# Revit family: WT02 RHO
name_source: partatom
category: Windows
revit_build: Autodesk Revit Architecture 2012 (Build: 20110916_2132(x64)
units: mm (PartAtom-declared; Revit-internal decimal feet)

## types (4) — shared parameters
Casement Width = 395 mm
Cavity Closer Depth = 85 mm  [stored 0.278871 ft]
Cavity Closer Offset from Ext = 102.5 mm
Cavity Closer Width = 50 mm  [stored 0.164042 ft]
Cill Depth = 87.5 mm
Default Head Height = 2110 mm
Frame Depth = 65 mm
FrameOffset - External = 50 mm  [stored 0.164042 ft]
Glazing Thickness = 24 mm
Height = 1360 mm  [stored 4.46194 ft]
Keynote = L10
Manufacturer = Revit
Material Frame = Window Frame
Material Glass = Glass
Material Trim = Window Frame
Operation = DoublePanelVertical
Precast Width = 150 mm
Rough Height = 1130 mm
Vis - Cavity Closers = Yes
Wall Closure = By host
Window Board Extension = 25 mm  [stored 0.082021 ft]
Window Board Projection = 25 mm  [stored 0.082021 ft]
Wrap Layers (Ext) from Ext = 102.5 mm
Wrap Layers (Int) from Ext = 177.5 mm
window width = 935 mm

## per-type parameters (varying)
| type | Rough Width | Width |
| 1360x1360mm | 1500 mm | 1500 mm |
| 1360x1360mm 2 | 1360 mm  [stored 4.46194 ft] | 1360 mm  [stored 4.46194 ft] |
| 1360x1360mm (test) | 1360 mm  [stored 4.46194 ft] | 1360 mm  [stored 4.46194 ft] |
| 1360x1360mm (WC Cell) | 1360 mm  [stored 4.46194 ft] | 1360 mm  [stored 4.46194 ft] |

note: [stored X ft] marks values corroborated as IEEE doubles in the binary element streams (Revit-internal decimal feet)

## geometry (parser evidence)
native form markers: Sweep x3
no freeform markers — native parametric forms only
